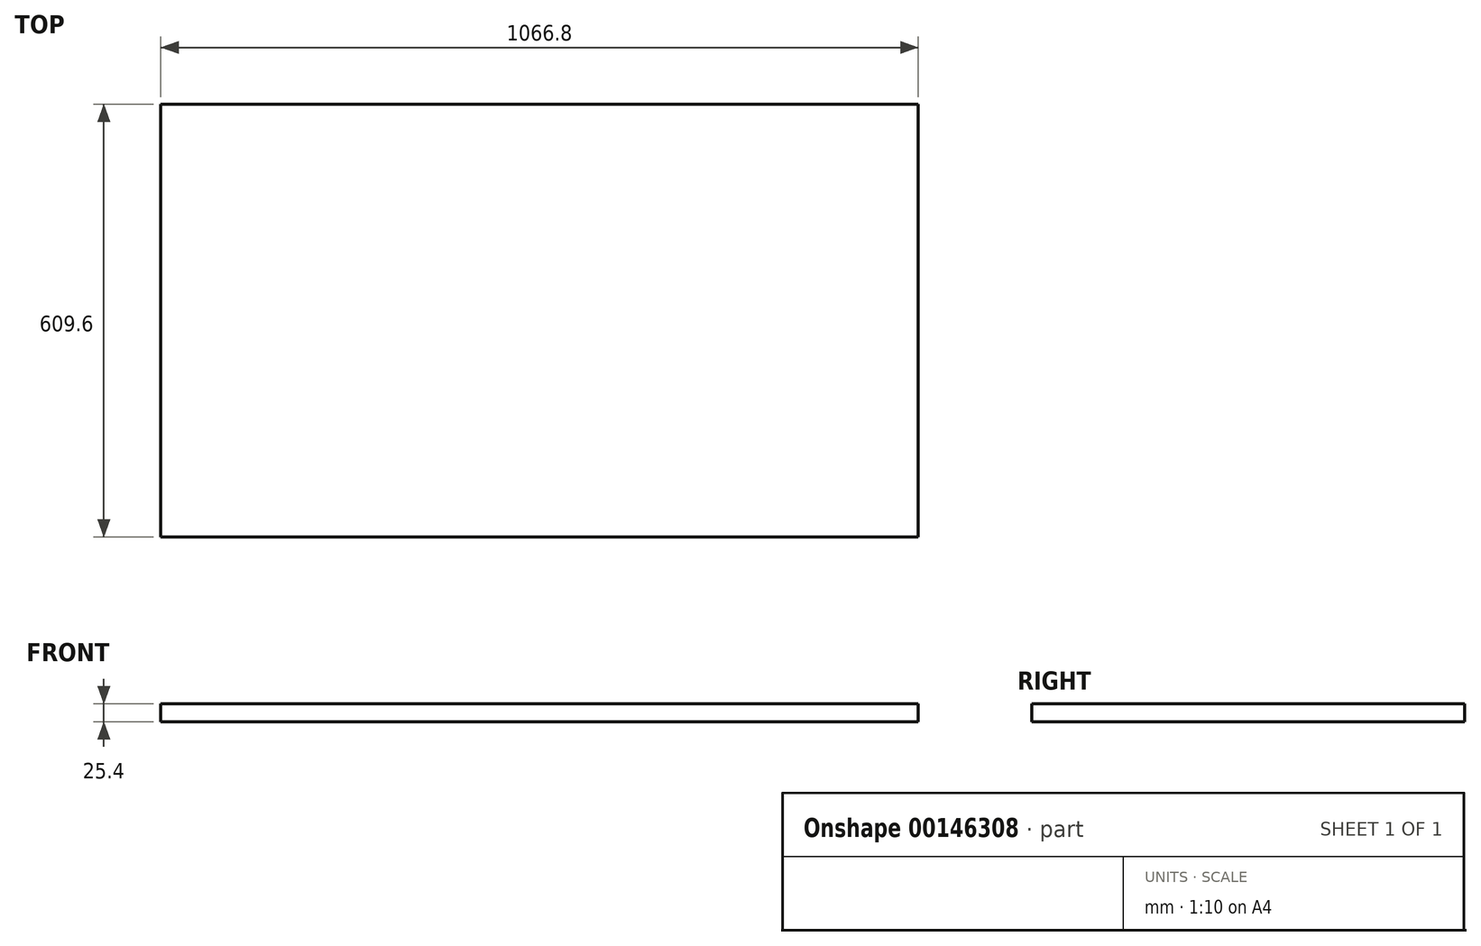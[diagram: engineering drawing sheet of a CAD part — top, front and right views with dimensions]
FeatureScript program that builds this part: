
annotation { "Feature Type Name" : "Feature", "Feature Type Description" : "" }
export const myFeature = defineFeature(function(context is Context, id is Id, definition is map)
    precondition{}
    {
        {
            var Q0;
            Q0=qCreatedBy(makeId("Top.planeOp"),FACE);
            var sketch = newSketch(context, id + "F0", { "sketchPlane" : qUnion([Q0])});
            skLineSegment(sketch, "E0.bottom", {"start": v(0, 0) * mm, "end": v(1066.8, 0) * mm});
            skLineSegment(sketch, "E0.top", {"start": v(0, 609.6) * mm, "end": v(1066.8, 609.6) * mm});
            skLineSegment(sketch, "E0.left", {"start": v(0, 0) * mm, "end": v(0, 609.6) * mm});
            skLineSegment(sketch, "E0.right", {"start": v(1066.8, 0) * mm, "end": v(1066.8, 609.6) * mm});
            skSolve(sketch);
        }
        {
            var Q0;
            Q0 = qSketchRegion(id + "F0", true);
            extrude(context, id + "F1", {"entities" : qUnion([Q0]), "depth" : 25.4 * mm});
        }
    });
